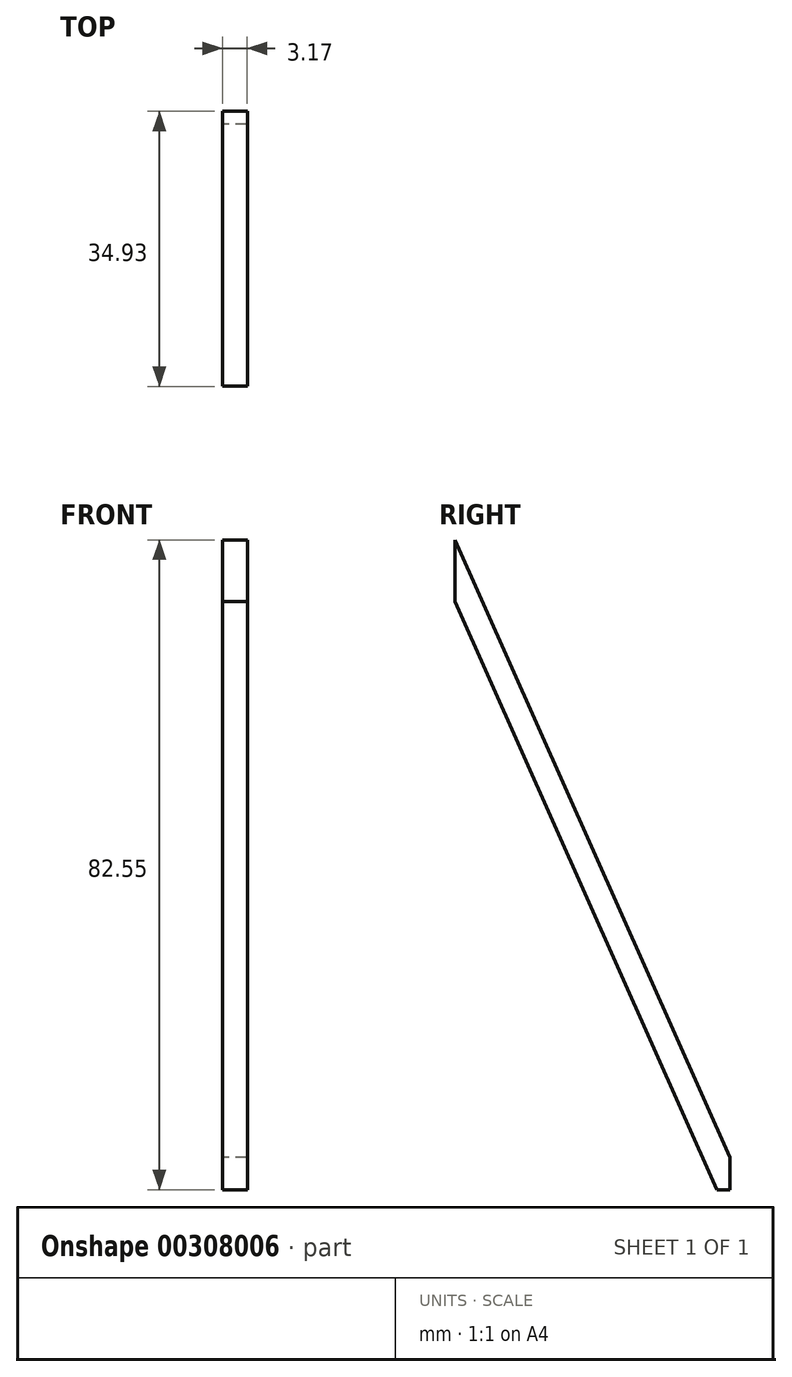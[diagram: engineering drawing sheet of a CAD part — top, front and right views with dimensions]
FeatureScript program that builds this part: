
annotation { "Feature Type Name" : "Feature", "Feature Type Description" : "" }
export const myFeature = defineFeature(function(context is Context, id is Id, definition is map)
    precondition{}
    {
        {
            var Q0;
            Q0=qCreatedBy(makeId("Right.planeOp"),FACE);
            var sketch = newSketch(context, id + "F0", { "sketchPlane" : qUnion([Q0])});
            skLineSegment(sketch, "E0", {"start": v(-33.28, 82.55) * mm, "end": v(1.65, 4.1) * mm});
            skLineSegment(sketch, "E1", {"start": v(1.65, 4.1) * mm, "end": v(1.65, 0) * mm});
            skLineSegment(sketch, "E2", {"start": v(0, 0) * mm, "end": v(-33.28, 74.74) * mm});
            skLineSegment(sketch, "E3", {"start": v(1.65, 0) * mm, "end": v(0, 0) * mm});
            skLineSegment(sketch, "E4", {"start": v(-33.28, 82.55) * mm, "end": v(-33.28, 74.74) * mm});
            skSolve(sketch);
        }
        {
            var Q0;
            {var subQ1=sQuery(id+"F0.wireOp",EDGE,"v7TPivB9-42B2-h8bl-C47S-AysVj0HJQgM8.bottom");Q0=makeQuery(id+"F0.imprint","IMPRINT",FACE,{"disambiguationData":[TD([[makeQuery(id+"F0.imprint","IMPRINT",EDGE,{"derivedFrom":subQ1}),1.0]])]});}
            var Q1;
            {var subQ1=sQuery(id+"F0.wireOp",EDGE,"E0");Q1=makeQuery(id+"F0.imprint","IMPRINT",FACE,{"disambiguationData":[TD([[makeQuery(id+"F0.imprint","IMPRINT",EDGE,{"derivedFrom":subQ1}),-1.0]])]});}
            extrude(context, id + "F1", {"entities" : qUnion([Q0, Q1]), "depth" : 3.17 * mm});
        }
    });
